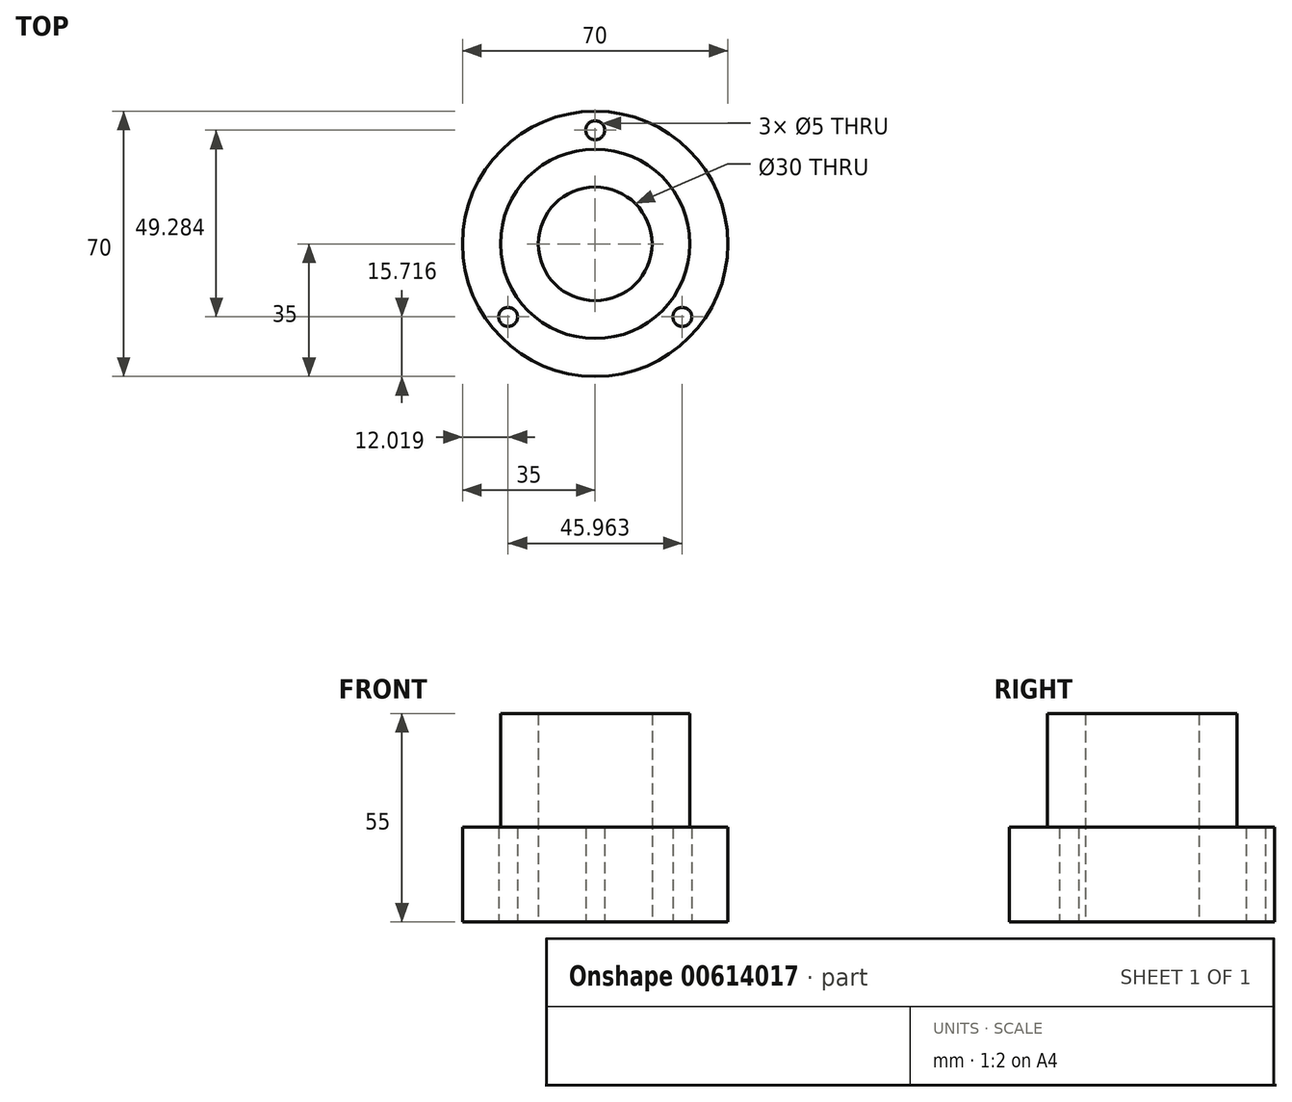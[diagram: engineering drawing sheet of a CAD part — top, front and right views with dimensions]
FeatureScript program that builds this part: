
annotation { "Feature Type Name" : "Feature", "Feature Type Description" : "" }
export const myFeature = defineFeature(function(context is Context, id is Id, definition is map)
    precondition{}
    {
        {
            var Q0;
            Q0=qCreatedBy(makeId("Top.planeOp"),FACE);
            var sketch = newSketch(context, id + "F0", { "sketchPlane" : qUnion([Q0])});
            skCircle(sketch, "E0", {"center": v(0, 0) * mm, "radius": 15 * mm});
            skCircle(sketch, "E1", {"center": v(0, 0) * mm, "radius": 25 * mm});
            skCircle(sketch, "E2", {"center": v(0, 0) * mm, "radius": 35 * mm});
            skCircle(sketch, "E3", {"center": v(0, 30) * mm, "radius": 2.5 * mm});
            skCircle(sketch, "E4", {"center": v(-22.98, -19.28) * mm, "radius": 2.5 * mm});
            skCircle(sketch, "E5", {"center": v(22.98, -19.28) * mm, "radius": 2.5 * mm});
            skCircle(sketch, "E6", {"center": v(0, 30) * mm, "radius": 1 * mm});
            skCircle(sketch, "E7", {"center": v(-22.98, -19.28) * mm, "radius": 1 * mm});
            skCircle(sketch, "E8", {"center": v(22.98, -19.28) * mm, "radius": 1 * mm});
            skSolve(sketch);
        }
        {
            var Q0;
            Q0 = qSketchRegion(id + "F0", true);
            extrude(context, id + "F1", {"entities" : qUnion([Q0]), "depth" : 25 * mm, "offsetDistance" : 25 * mm});
        }
        {
            var Q0;
            Q0=makeQuery(id+"F0.imprint","IMPRINT",FACE,{"disambiguationData":[TD([[makeQuery(id+"F0.imprint","IMPRINT",EDGE,{"derivedFrom":sQuery(id+"F0.wireOp",EDGE,"E0")}),-1.0]])]});
            extrude(context, id + "F2", {"entities" : qUnion([Q0]), "operationType" : NewBodyOperationType.ADD, "depth" : 55 * mm, "offsetDistance" : 25 * mm});
        }
        {
            var Q0;
            Q0=sQuery(id+"F0.wireOp",EDGE,"E3");
            var Q1;
            Q1=sQuery(id+"F0.wireOp",EDGE,"E4");
            var Q2;
            Q2=sQuery(id+"F0.wireOp",EDGE,"E5");
            extrude(context, id + "F3", {"bodyType" : ToolBodyType.SURFACE, "surfaceEntities" : qUnion([Q0, Q1, Q2]), "depth" : 5 * mm, "offsetDistance" : 25 * mm});
        }
    });
